# Revit family: Power_Module-Lutron-Lumaris-LU-PS3-A_1 (1)
name_source: partatom
category: Lighting Devices
units: mm (PartAtom-declared; Revit-internal decimal feet)

## family parameters
Cut with Voids When Loaded = No
Host = Face
Maintain Annotation Orientation = Yes
OmniClass Number = 23.85.80.11.27
OmniClass Title = Lighting Controls
Part Type = Switch
Room Calculation Point = No
Round Connector Dimension = Use Diameter
Shared = No

## types (1)
- LU-PH3-A
    Apparent Load = 0 VA
    Assembly Code = D5090900
    Cost = 0 $
    Default Elevation = 5' - 0"
    Description = LED Power module
    Environment = Ambient operating temperature: 32 °F to 104 °F
(0 °C to 40 °C)
    Finish = Metal - Lutron - Silver
    Instruction Sheet Link = https://assets.lutron.com
    Load Classification = Lighting
    Manufacturer = Lutron Electronics Co., Inc
    Manufacturer Fax Number = 610-282-1243
    Material = Contact Manufacturer for More Information
    Model = LU-PH3-A
    Number of Poles = 1
    Overall Depth = 0' - 2"
    Overall Height = 0' - 10 1/2"
    Overall Width = 0' - 5 1/2"
    Performance URL = http://www.lutron.com
    Power Factor = 1
    Product Documentation Link = https://assets.lutron.com
    Product Name = Power Interface Enclosure
    Product Page URL = https://luxury.lutron.com
    Series = Lumaris Tunable White Tape Light
    URL = http://www.lutron.com
    Version = 2021 - v1.0a
    Video Link = https://www.youtube.com
    Voltage = 220 V
    Voltage Comment = Must be permanently connected fixed wiring for 277 V~
application.
    Warranty URL = http://www.lutron.com

## geometry (parser evidence)
native form markers: Sweep x2
no freeform markers — native parametric forms only
